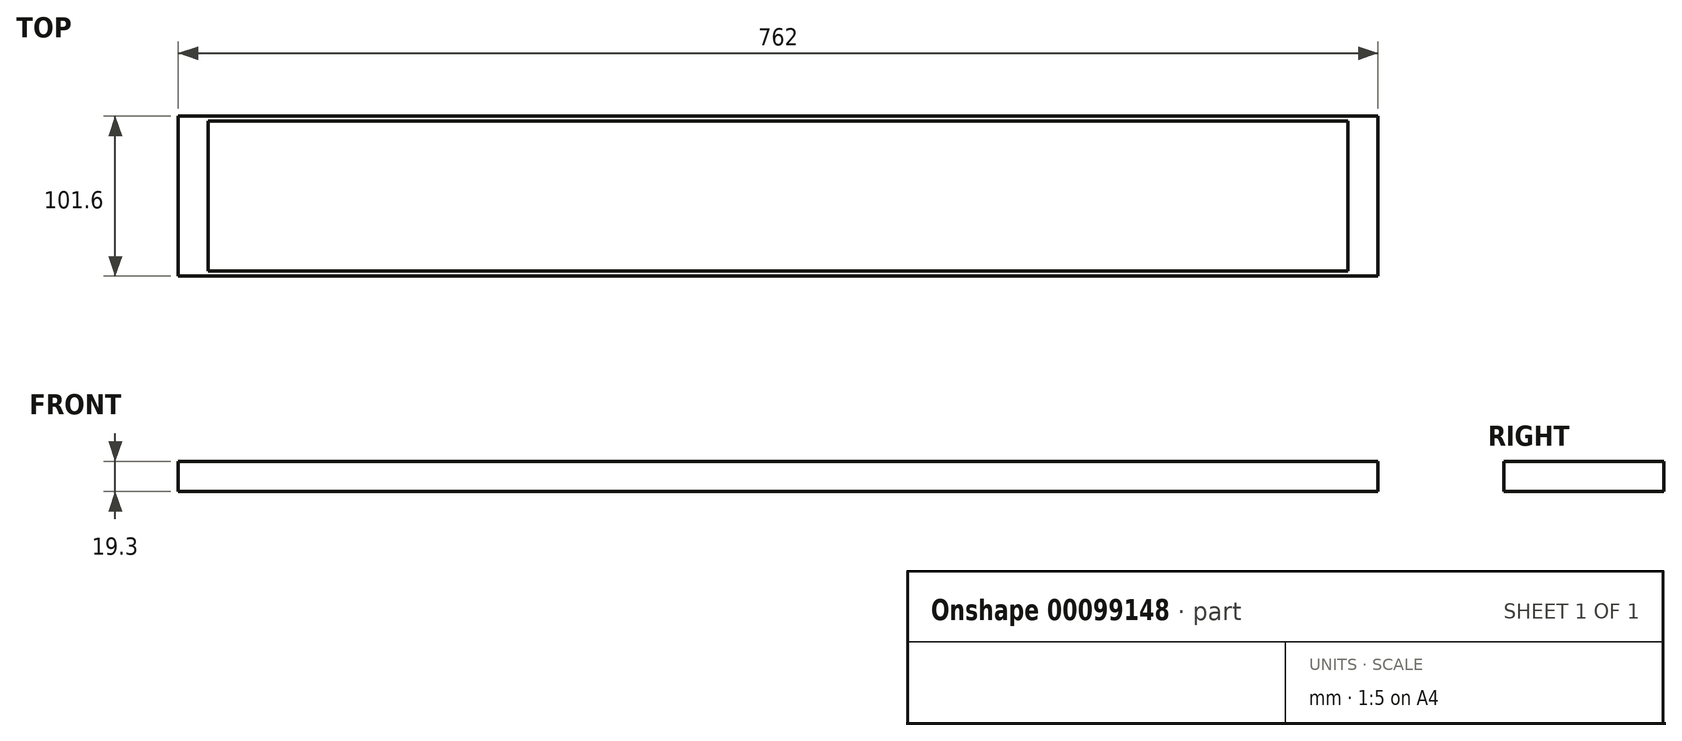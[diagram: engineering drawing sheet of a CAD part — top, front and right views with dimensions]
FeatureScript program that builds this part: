
annotation { "Feature Type Name" : "Feature", "Feature Type Description" : "" }
export const myFeature = defineFeature(function(context is Context, id is Id, definition is map)
    precondition{}
    {
        {
            var Q0;
            Q0=qCreatedBy(makeId("Top.planeOp"),FACE);
            var sketch = newSketch(context, id + "F0", { "sketchPlane" : qUnion([Q0])});
            skLineSegment(sketch, "E0.bottom", {"start": v(381, 50.8) * mm, "end": v(-381, 50.8) * mm});
            skLineSegment(sketch, "E0.top", {"start": v(381, -50.8) * mm, "end": v(-381, -50.8) * mm});
            skLineSegment(sketch, "E0.left", {"start": v(381, 50.8) * mm, "end": v(381, -50.8) * mm});
            skLineSegment(sketch, "E0.right", {"start": v(-381, 50.8) * mm, "end": v(-381, -50.8) * mm});
            skPoint(sketch, "E0.middle", {"position": v(0, 0) * mm});
            skSolve(sketch);
        }
        {
            var Q0;
            Q0=makeQuery(id+"F0.imprint","IMPRINT",FACE,{"disambiguationData":[TD([[makeQuery(id+"F0.imprint","IMPRINT",EDGE,{"derivedFrom":sQuery(id+"F0.wireOp",EDGE,"E0.bottom")}),1.0]])]});
            extrude(context, id + "F1", {"entities" : qUnion([Q0]), "depth" : 19.05 * mm});
        }
        {
            var Q0;
            Q0=makeQuery(id+"F1.opExtrude","CAP_FACE",FACE,{"disambiguationData":[OSD([sQuery(id+"F0.wireOp",EDGE,"E0.bottom"),sQuery(id+"F0.wireOp",EDGE,"E0.top"),sQuery(id+"F0.wireOp",EDGE,"E0.left"),sQuery(id+"F0.wireOp",EDGE,"E0.right")])],"isStart":false});
            var sketch = newSketch(context, id + "F2", { "sketchPlane" : qUnion([Q0])});
            skPoint(sketch, "E1", {"position": v(-361.95, 47.63) * mm});
            skPoint(sketch, "E2", {"position": v(361.95, -47.63) * mm});
            skLineSegment(sketch, "E3.bottom", {"start": v(-361.95, 47.63) * mm, "end": v(361.95, 47.63) * mm});
            skLineSegment(sketch, "E3.top", {"start": v(-361.95, -47.63) * mm, "end": v(361.95, -47.63) * mm});
            skLineSegment(sketch, "E3.left", {"start": v(-361.95, 47.63) * mm, "end": v(-361.95, -47.63) * mm});
            skLineSegment(sketch, "E3.right", {"start": v(361.95, 47.63) * mm, "end": v(361.95, -47.63) * mm});
            skSolve(sketch);
        }
        {
            var Q0;
            Q0=makeQuery(id+"F2.imprint","IMPRINT",FACE,{"disambiguationData":[TD([[makeQuery(id+"F2.imprint","IMPRINT",EDGE,{"derivedFrom":sQuery(id+"F2.wireOp",EDGE,"E3.bottom")}),-1.0]])]});
            extrude(context, id + "F3", {"entities" : qUnion([Q0]), "operationType" : NewBodyOperationType.ADD, "depth" : 0.25 * mm});
        }
    });
